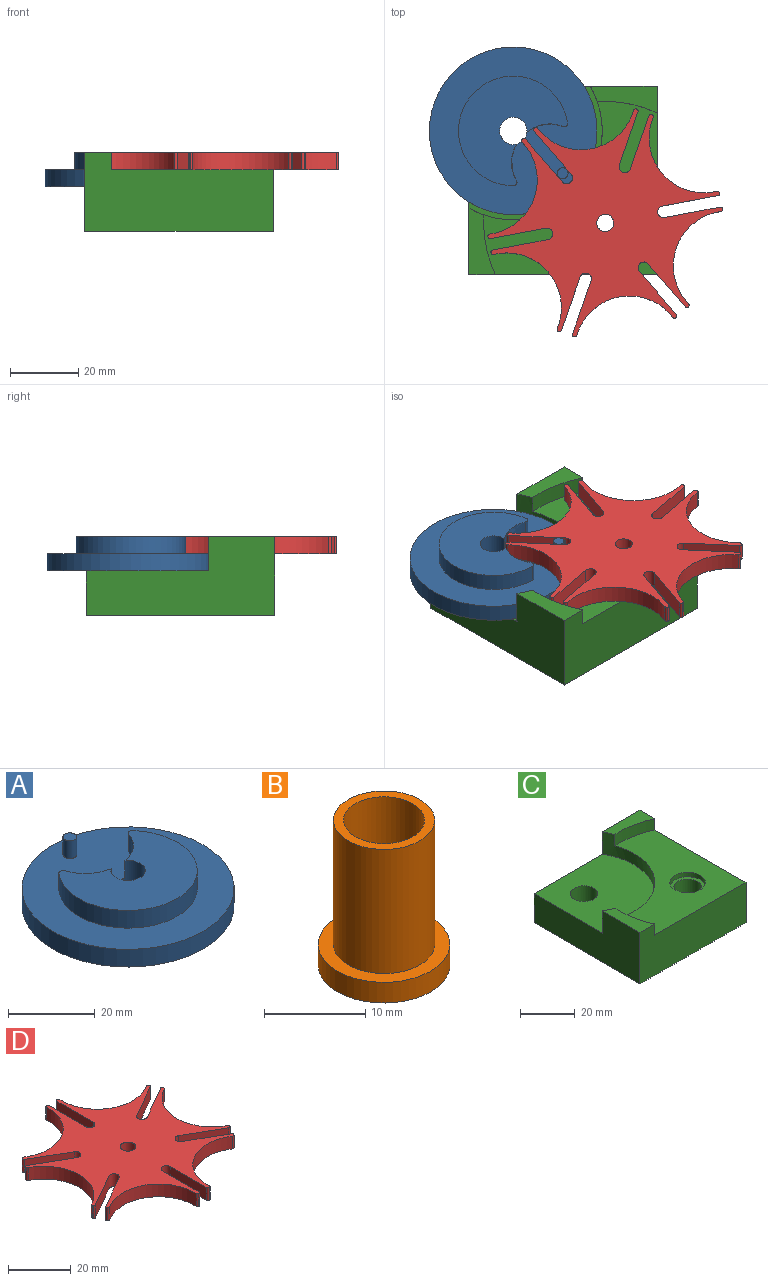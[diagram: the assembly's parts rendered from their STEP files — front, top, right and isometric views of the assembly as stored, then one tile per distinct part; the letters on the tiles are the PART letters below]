
ASSEMBLY  parts=4 mates=4
PART A: 12 faces, bbox 49x49x10 mm
  f0: plane 49x49mm, normal (0,0,1), area 1278.1mm2, adj f1,f2,f4,f5,f6,f8,f10,f11
  f1: cylinder r=24.5mm len=49mm, axis (0,0,-1), area 769.7mm2, adj f0,f3
  f2: cylinder r=4mm len=10mm, axis (0,0,-1), area 227mm2, adj f0,f3,f4,f6,f7
  f3: plane 49x49mm, normal (0,0,-1), area 1835.5mm2, adj f1,f2
  f4: extruded ~8.07x6.87mm, area 55.8mm2, adj f0,f2,f7,f10
  f5: cylinder r=16mm len=32mm, axis (0,0,-1), area 366mm2, adj f0,f7,f10,f11
  f6: extruded ~8.07x6.87mm, area 55.8mm2, adj f0,f2,f7,f11
  f7: plane 32x26.86mm, normal (0,0,1), area 549.3mm2, adj f2,f4,f5,f6,f10,f11
  f8: cylinder r=1.6mm len=5mm, axis (0,0,-1), area 50.3mm2, adj f0,f9
  f9: plane 3.2x3.2mm, normal (0,0,1), area 8mm2, adj f8
  f10: cylinder r=1mm len=5mm, axis (0,0,-1), area 10.6mm2, adj f0,f4,f5,f7
  f11: cylinder r=1mm len=5mm, axis (0,0,-1), area 10.6mm2, adj f0,f5,f6,f7
PART B: 6 faces, bbox 13x13x17.5 mm
  f0: cylinder r=4mm len=17.5mm, axis (0,0,-1), area 439.8mm2, adj f2,f4
  f1: cylinder r=5mm len=15mm, axis (0,0,-1), area 471.2mm2, adj f2,f5
  f2: plane 10x10mm, normal (0,0,1), area 28.3mm2, adj f0,f1
  f3: cylinder r=6.5mm len=13mm, axis (0,0,1), area 102.1mm2, adj f4,f5
  f4: plane 13x13mm, normal (0,0,-1), area 82.5mm2, adj f0,f3
  f5: plane 13x13mm, normal (0,0,1), area 54.2mm2, adj f1,f3
PART C: 16 faces, bbox 55x55x23 mm
  f0: cylinder r=5mm len=16mm, axis (0,0,-1), area 502.7mm2, adj f5,f15
  f1: plane 55x23mm, normal (-1,0,0), area 909.9mm2, adj f2,f4,f5,f6,f7,f11
  f2: plane 55x23mm, normal (0,1,0), area 909.9mm2, adj f1,f4,f5,f6,f8,f13
  f3: cylinder r=5mm len=13mm, axis (0,0,-1), area 408.4mm2, adj f4,f5
  f4: plane 38.97x38.97mm, normal (0,0,1), area 1266.1mm2, adj f1,f2,f3,f6
  f5: plane 55x55mm, normal (0,0,-1), area 2867.9mm2, adj f0,f1,f2,f3,f7,f8
  f6: cylinder r=26mm len=38.97mm, axis (0,0,-1), area 388.7mm2, adj f1,f2,f4,f9,f10,f11,f12,f13
  f7: plane 55x23mm, normal (0,-1,0), area 1028.7mm2, adj f1,f5,f8,f9,f10,f11
  f8: plane 55x23mm, normal (1,0,0), area 1028.7mm2, adj f2,f5,f7,f9,f12,f13
  f9: plane 50.66x50.66mm, normal (0,0,1), area 1353.8mm2, adj f6,f7,f8,f10,f12,f14
  f10: cylinder r=35.5mm len=17.47mm, axis (0,0,-1), area 89.9mm2, adj f6,f7,f9,f11
  f11: plane 19.49x7.74mm, normal (0,0,1), area 96.9mm2, adj f1,f6,f7,f10
  f12: cylinder r=35.5mm len=17.47mm, axis (0,0,-1), area 89.9mm2, adj f6,f8,f9,f13
  f13: plane 19.49x7.74mm, normal (0,0,1), area 96.9mm2, adj f2,f6,f8,f12
  f14: cylinder r=6.5mm len=13mm, axis (0,0,1), area 81.7mm2, adj f9,f15
  f15: plane 13x13mm, normal (0,0,1), area 54.2mm2, adj f0,f14
PART D: 63 faces, bbox 62.2x68.8x5 mm
  f0: cylinder r=16mm len=24.74mm, axis (0,0,-1), area 176.3mm2, adj f37,f38,f39,f62
  f1: cylinder r=34.5mm len=5mm, axis (0,0,-1), area 0.6mm2, adj f37,f38,f39,f40
  f2: plane 14.29x8.25mm, normal (-0.5,-0.87,0), area 82.5mm2, adj f3,f37,f38,f40
  f3: cylinder r=1.7mm len=5mm, axis (0,0,-1), area 26.7mm2, adj f2,f4,f37,f38
  f4: plane 14.29x8.25mm, normal (0.5,0.87,0), area 82.5mm2, adj f3,f37,f38,f41
  f5: cylinder r=34.5mm len=5mm, axis (0,0,-1), area 0.6mm2, adj f37,f38,f41,f42
  f6: cylinder r=16mm len=28.54mm, axis (0,0,-1), area 176.3mm2, adj f37,f38,f42,f43
  f7: cylinder r=34.5mm len=5mm, axis (0,0,-1), area 0.6mm2, adj f37,f38,f43,f44
  f8: plane 14.29x8.25mm, normal (0.5,-0.87,0), area 82.5mm2, adj f9,f37,f38,f44
  f9: cylinder r=1.7mm len=5mm, axis (0,0,-1), area 26.7mm2, adj f8,f10,f37,f38
  f10: plane 14.29x8.25mm, normal (-0.5,0.87,0), area 82.5mm2, adj f9,f37,f38,f45
  f11: cylinder r=34.5mm len=5mm, axis (0,0,-1), area 0.6mm2, adj f37,f38,f45,f46
  f12: cylinder r=16mm len=24.74mm, axis (0,0,-1), area 176.3mm2, adj f37,f38,f46,f47
  f13: cylinder r=34.5mm len=5mm, axis (0,0,-1), area 0.6mm2, adj f37,f38,f47,f48
  f14: plane 16.5x5mm, normal (1,0,0), area 82.5mm2, adj f15,f37,f38,f48
  f15: cylinder r=1.7mm len=5mm, axis (0,0,-1), area 26.7mm2, adj f14,f16,f37,f38
  f16: plane 16.5x5mm, normal (-1,0,0), area 82.5mm2, adj f15,f37,f38,f49
  f17: cylinder r=34.5mm len=5mm, axis (0,0,-1), area 0.6mm2, adj f37,f38,f49,f50
  f18: cylinder r=16mm len=24.74mm, axis (0,0,-1), area 176.3mm2, adj f37,f38,f50,f51
  f19: cylinder r=34.5mm len=5mm, axis (0,0,-1), area 0.6mm2, adj f37,f38,f51,f52
  f20: plane 14.29x8.25mm, normal (0.5,0.87,0), area 82.5mm2, adj f21,f37,f38,f52
  f21: cylinder r=1.7mm len=5mm, axis (0,0,-1), area 26.7mm2, adj f20,f22,f37,f38
  f22: plane 14.29x8.25mm, normal (-0.5,-0.87,0), area 82.5mm2, adj f21,f37,f38,f53
  f23: cylinder r=34.5mm len=5mm, axis (0,0,-1), area 0.6mm2, adj f37,f38,f53,f54
  f24: cylinder r=16mm len=28.54mm, axis (0,0,-1), area 176.3mm2, adj f37,f38,f54,f55
  f25: cylinder r=34.5mm len=5mm, axis (0,0,-1), area 0.6mm2, adj f37,f38,f55,f56
  f26: plane 14.29x8.25mm, normal (-0.5,0.87,0), area 82.5mm2, adj f27,f37,f38,f56
  f27: cylinder r=1.7mm len=5mm, axis (0,0,-1), area 26.7mm2, adj f26,f28,f37,f38
  f28: plane 14.29x8.25mm, normal (0.5,-0.87,0), area 82.5mm2, adj f27,f37,f38,f57
  f29: cylinder r=34.5mm len=5mm, axis (0,0,-1), area 0.6mm2, adj f37,f38,f57,f58
  f30: cylinder r=16mm len=24.74mm, axis (0,0,-1), area 176.3mm2, adj f37,f38,f58,f59
  f31: cylinder r=34.5mm len=5mm, axis (0,0,-1), area 0.6mm2, adj f37,f38,f59,f60
  f32: plane 16.5x5mm, normal (-1,0,0), area 82.5mm2, adj f33,f37,f38,f60
  f33: cylinder r=1.7mm len=5mm, axis (0,0,-1), area 26.7mm2, adj f32,f34,f37,f38
  f34: plane 16.5x5mm, normal (1,0,0), area 82.5mm2, adj f33,f37,f38,f61
  f35: cylinder r=34.5mm len=5mm, axis (0,0,-1), area 0.6mm2, adj f37,f38,f61,f62
  f36: cylinder r=2.5mm len=5mm, axis (0,0,-1), area 78.5mm2, adj f37,f38
  f37: plane 68.84x62.19mm, normal (0,0,1), area 1800.2mm2, adj f0,f1,f2,f3,f4,f5,f6,f7
  f38: plane 68.84x62.19mm, normal (0,0,-1), area 1800.2mm2, adj f0,f1,f2,f3,f4,f5,f6,f7
  f39: cylinder r=0.6mm len=5mm, axis (0,0,1), area 4.7mm2, adj f0,f1,f37,f38
  f40: cylinder r=0.6mm len=5mm, axis (0,0,-1), area 4.9mm2, adj f1,f2,f37,f38
  f41: cylinder r=0.6mm len=5mm, axis (0,0,-1), area 4.9mm2, adj f4,f5,f37,f38
  f42: cylinder r=0.6mm len=5mm, axis (0,0,1), area 4.7mm2, adj f5,f6,f37,f38
  f43: cylinder r=0.6mm len=5mm, axis (0,0,1), area 4.7mm2, adj f6,f7,f37,f38
  f44: cylinder r=0.6mm len=5mm, axis (0,0,-1), area 4.9mm2, adj f7,f8,f37,f38
  f45: cylinder r=0.6mm len=5mm, axis (0,0,-1), area 4.9mm2, adj f10,f11,f37,f38
  f46: cylinder r=0.6mm len=5mm, axis (0,0,1), area 4.7mm2, adj f11,f12,f37,f38
  f47: cylinder r=0.6mm len=5mm, axis (0,0,1), area 4.7mm2, adj f12,f13,f37,f38
  f48: cylinder r=0.6mm len=5mm, axis (0,0,-1), area 4.9mm2, adj f13,f14,f37,f38
  f49: cylinder r=0.6mm len=5mm, axis (0,0,-1), area 4.9mm2, adj f16,f17,f37,f38
  f50: cylinder r=0.6mm len=5mm, axis (0,0,1), area 4.7mm2, adj f17,f18,f37,f38
  f51: cylinder r=0.6mm len=5mm, axis (0,0,1), area 4.7mm2, adj f18,f19,f37,f38
  f52: cylinder r=0.6mm len=5mm, axis (0,0,-1), area 4.9mm2, adj f19,f20,f37,f38
  f53: cylinder r=0.6mm len=5mm, axis (0,0,-1), area 4.9mm2, adj f22,f23,f37,f38
  f54: cylinder r=0.6mm len=5mm, axis (0,0,1), area 4.7mm2, adj f23,f24,f37,f38
  f55: cylinder r=0.6mm len=5mm, axis (0,0,1), area 4.7mm2, adj f24,f25,f37,f38
  f56: cylinder r=0.6mm len=5mm, axis (0,0,-1), area 4.9mm2, adj f25,f26,f37,f38
  f57: cylinder r=0.6mm len=5mm, axis (0,0,-1), area 4.9mm2, adj f28,f29,f37,f38
  f58: cylinder r=0.6mm len=5mm, axis (0,0,1), area 4.7mm2, adj f29,f30,f37,f38
  f59: cylinder r=0.6mm len=5mm, axis (0,0,1), area 4.7mm2, adj f30,f31,f37,f38
  f60: cylinder r=0.6mm len=5mm, axis (0,0,-1), area 4.9mm2, adj f31,f32,f37,f38
  f61: cylinder r=0.6mm len=5mm, axis (0,0,-1), area 4.9mm2, adj f34,f35,f37,f38
  f62: cylinder r=0.6mm len=5mm, axis (0,0,1), area 4.7mm2, adj f0,f35,f37,f38
PLACE A rot(axis=(0,0,-1),130.7deg) t=(-14.53,14.53,13)mm
PLACE B rot(axis=(1,0,0),180deg) t=(65.75,-27.17,16)mm
PLACE C at identity fixed
PLACE D rot(axis=(0,0,1),40.7deg) t=(12.34,-12.34,18)mm
MATE revolute A.f1 <-> C.f3  axis (0,0,-1) through (-14.53,14.53,13)mm
MATE pin_slot A.f8 <-> D.f33  axis (0,0,1) through (-0.12,2.14,23)mm
MATE revolute D.f36 <-> C.f0  axis (0,0,-1) through (12.34,-12.34,18)mm
MATE fastened B.f0 <-> C.f0  axis (0,0,-1) through (12.34,-12.34,16)mm
